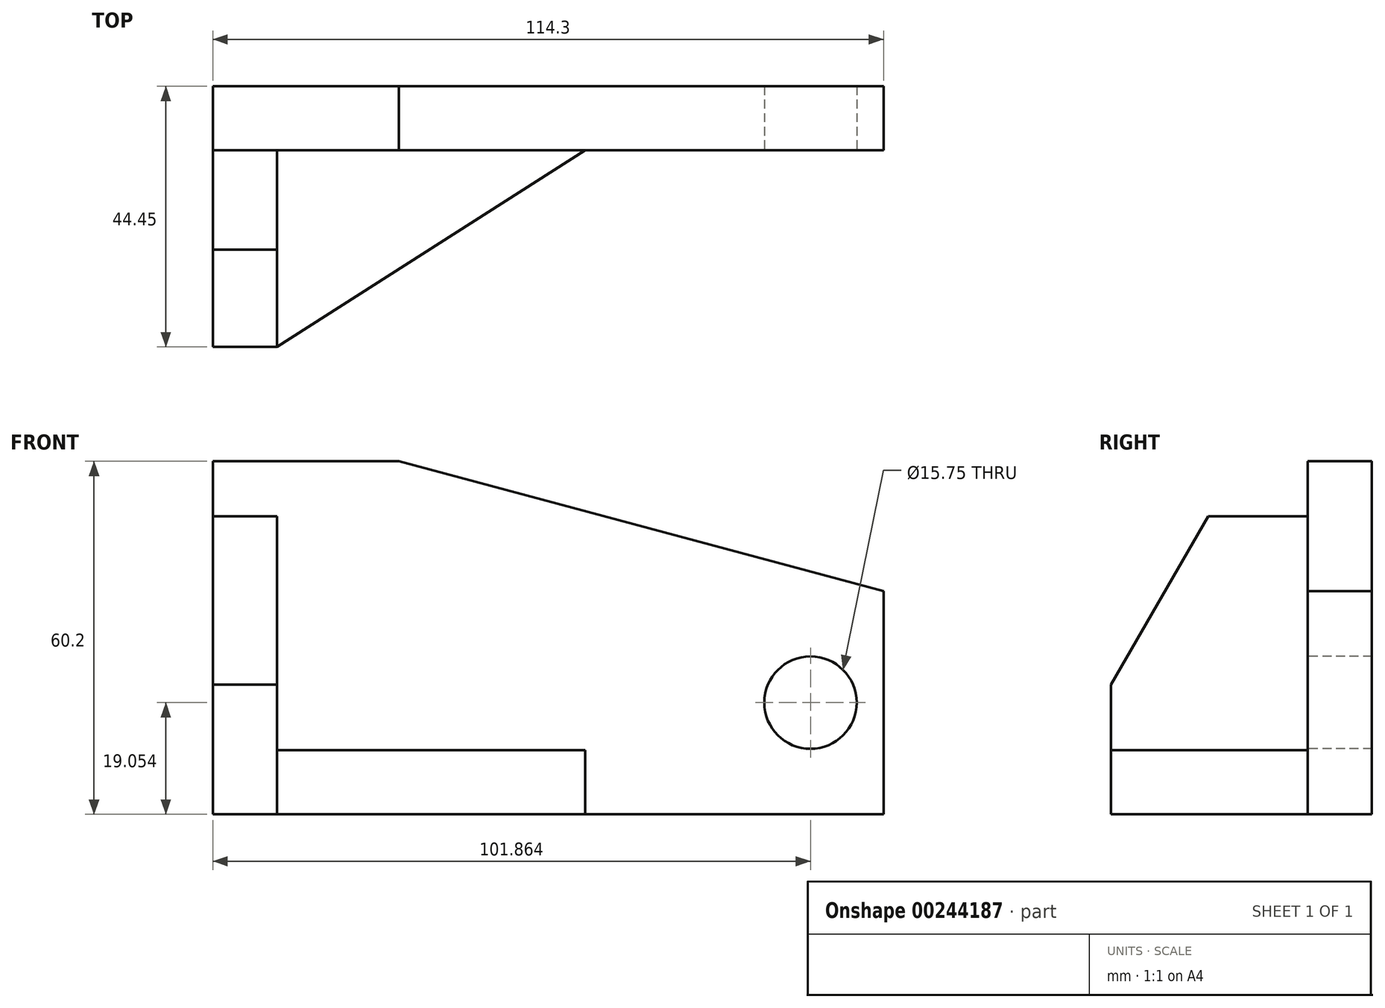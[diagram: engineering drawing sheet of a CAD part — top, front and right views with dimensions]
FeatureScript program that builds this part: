
annotation { "Feature Type Name" : "Feature", "Feature Type Description" : "" }
export const myFeature = defineFeature(function(context is Context, id is Id, definition is map)
    precondition{}
    {
        {
            var Q0;
            Q0=qCreatedBy(makeId("Front.planeOp"),FACE);
            var sketch = newSketch(context, id + "F0", { "sketchPlane" : qUnion([Q0])});
            skLineSegment(sketch, "E0.bottom", {"start": v(-54.26, 27.67) * mm, "end": v(-22.5, 27.67) * mm});
            skLineSegment(sketch, "E0.top", {"start": v(-54.26, -32.53) * mm, "end": v(60.04, -32.53) * mm});
            skLineSegment(sketch, "E0.left", {"start": v(-54.26, 27.67) * mm, "end": v(-54.26, -32.53) * mm});
            skLineSegment(sketch, "E0.right", {"start": v(60.04, 5.55) * mm, "end": v(60.04, -32.53) * mm});
            skLineSegment(sketch, "E1", {"start": v(-22.5, 27.67) * mm, "end": v(60.04, 5.55) * mm});
            skPoint(sketch, "E2.orphan", {"position": v(60.04, 27.67) * mm});
            skSolve(sketch);
        }
        {
            var Q0;
            Q0=makeQuery(id+"F0.imprint","IMPRINT",FACE,{"disambiguationData":[TD([[makeQuery(id+"F0.imprint","IMPRINT",EDGE,{"derivedFrom":sQuery(id+"F0.wireOp",EDGE,"E0.bottom")}),-1.0]])]});
            extrude(context, id + "F1", {"entities" : qUnion([Q0]), "depth" : 10.92 * mm});
        }
        {
            var Q0;
            Q0=makeQuery(id+"F1.opExtrude","CAP_FACE",FACE,{"disambiguationData":[OSD([sQuery(id+"F0.wireOp",EDGE,"E0.bottom"),sQuery(id+"F0.wireOp",EDGE,"E0.top"),sQuery(id+"F0.wireOp",EDGE,"E0.left"),sQuery(id+"F0.wireOp",EDGE,"E0.right"),sQuery(id+"F0.wireOp",EDGE,"E1")])],"isStart":false});
            var sketch = newSketch(context, id + "F2", { "sketchPlane" : qUnion([Q0])});
            skLineSegment(sketch, "E3.bottom", {"start": v(-54.26, 18.27) * mm, "end": v(-43.34, 18.27) * mm});
            skLineSegment(sketch, "E3.top", {"start": v(-54.26, -32.53) * mm, "end": v(-43.34, -32.53) * mm});
            skLineSegment(sketch, "E3.left", {"start": v(-54.26, 18.27) * mm, "end": v(-54.26, -32.53) * mm});
            skLineSegment(sketch, "E3.right", {"start": v(-43.34, 18.27) * mm, "end": v(-43.34, -32.53) * mm});
            skSolve(sketch);
        }
        {
            var Q0;
            Q0=makeQuery(id+"F2.imprint","IMPRINT",FACE,{"disambiguationData":[TD([[makeQuery(id+"F2.imprint","IMPRINT",EDGE,{"derivedFrom":sQuery(id+"F2.wireOp",EDGE,"E3.bottom")}),-1.0]])]});
            extrude(context, id + "F3", {"entities" : qUnion([Q0]), "operationType" : NewBodyOperationType.ADD, "depth" : 33.53 * mm});
        }
        {
            var Q0;
            Q0=makeQuery(id+"F3.opExtrude","SWEPT_FACE",FACE,{"disambiguationData":[OSD([sQuery(id+"F2.wireOp",EDGE,"E3.right")])]});
            var sketch = newSketch(context, id + "F4", { "sketchPlane" : qUnion([Q0])});
            skLineSegment(sketch, "E4", {"start": v(-44.45, -10.43) * mm, "end": v(-27.83, 18.36) * mm});
            skSolve(sketch);
        }
        {
            var Q0;
            {var subQ0=sQuery(id+"F4.wireOp",EDGE,"E4");var subQ1=sQuery(id+"F2.wireOp",EDGE,"E3.right");var subQ2=makeQuery(id+"F3.opExtrude","CAP_EDGE",EDGE,{"disambiguationData":[OSD([subQ1])],"isStart":false});var subQ3=makeQuery(id+"F4.imprint","INTERSECT",VERTEX,{"derivedFrom":[subQ2,subQ0]});Q0=makeQuery(id+"F4.imprint","IMPRINT",FACE,{"disambiguationData":[TD([[makeQuery(id+"F4.imprint","IMPRINT",EDGE,{"disambiguationData":[TD([[subQ3,-1.0]])],"derivedFrom":subQ0}),1.0]])]});}
            extrude(context, id + "F5", {"entities" : qUnion([Q0]), "operationType" : NewBodyOperationType.REMOVE, "oppositeDirection" : true, "depth" : 25.4 * mm});
        }
        {
            var Q0;
            Q0=makeQuery(id+"F1.opExtrude","CAP_FACE",FACE,{"disambiguationData":[OSD([sQuery(id+"F0.wireOp",EDGE,"E0.bottom"),sQuery(id+"F0.wireOp",EDGE,"E0.top"),sQuery(id+"F0.wireOp",EDGE,"E0.left"),sQuery(id+"F0.wireOp",EDGE,"E0.right"),sQuery(id+"F0.wireOp",EDGE,"E1")])],"isStart":false});
            var sketch = newSketch(context, id + "F6", { "sketchPlane" : qUnion([Q0])});
            skLineSegment(sketch, "E5.bottom", {"start": v(-43.34, -32.53) * mm, "end": v(9.24, -32.53) * mm});
            skLineSegment(sketch, "E5.top", {"start": v(-43.34, -21.6) * mm, "end": v(9.24, -21.6) * mm});
            skLineSegment(sketch, "E5.left", {"start": v(-43.34, -32.53) * mm, "end": v(-43.34, -21.6) * mm});
            skLineSegment(sketch, "E5.right", {"start": v(9.24, -32.53) * mm, "end": v(9.24, -21.6) * mm});
            skSolve(sketch);
        }
        {
            var Q0;
            Q0=makeQuery(id+"F6.imprint","IMPRINT",FACE,{"disambiguationData":[TD([[makeQuery(id+"F6.imprint","IMPRINT",EDGE,{"derivedFrom":sQuery(id+"F6.wireOp",EDGE,"E5.bottom")}),1.0]])]});
            extrude(context, id + "F7", {"entities" : qUnion([Q0]), "operationType" : NewBodyOperationType.ADD, "depth" : 33.53 * mm});
        }
        {
            var Q0;
            Q0=makeQuery(id+"F7.opExtrude","SWEPT_FACE",FACE,{"disambiguationData":[OSD([sQuery(id+"F6.wireOp",EDGE,"E5.top")])]});
            var sketch = newSketch(context, id + "F8", { "sketchPlane" : qUnion([Q0])});
            skLineSegment(sketch, "E6", {"start": v(9.24, -10.92) * mm, "end": v(-43.34, -44.45) * mm});
            skSolve(sketch);
        }
        {
            var Q0;
            Q0=makeQuery(id+"F8.imprint","IMPRINT",FACE,{"disambiguationData":[TD([[makeQuery(id+"F8.imprint","IMPRINT",EDGE,{"derivedFrom":sQuery(id+"F8.wireOp",EDGE,"E6")}),1.0]])]});
            extrude(context, id + "F9", {"entities" : qUnion([Q0]), "operationType" : NewBodyOperationType.REMOVE, "oppositeDirection" : true, "depth" : 10.92 * mm});
        }
        {
            var Q0;
            Q0=makeQuery(id+"F1.opExtrude","CAP_FACE",FACE,{"disambiguationData":[OSD([sQuery(id+"F0.wireOp",EDGE,"E0.bottom"),sQuery(id+"F0.wireOp",EDGE,"E0.top"),sQuery(id+"F0.wireOp",EDGE,"E0.left"),sQuery(id+"F0.wireOp",EDGE,"E0.right"),sQuery(id+"F0.wireOp",EDGE,"E1")])],"isStart":false});
            var sketch = newSketch(context, id + "F10", { "sketchPlane" : qUnion([Q0])});
            skCircle(sketch, "E7", {"center": v(47.6, -13.48) * mm, "radius": 7.87 * mm});
            skSolve(sketch);
        }
        {
            var Q0;
            Q0=makeQuery(id+"F10.imprint","IMPRINT",FACE,{"disambiguationData":[TD([[makeQuery(id+"F10.imprint","IMPRINT",EDGE,{"derivedFrom":sQuery(id+"F10.wireOp",EDGE,"E7")}),1.0]])]});
            extrude(context, id + "F11", {"entities" : qUnion([Q0]), "operationType" : NewBodyOperationType.REMOVE, "oppositeDirection" : true, "depth" : 10.92 * mm});
        }
    });
